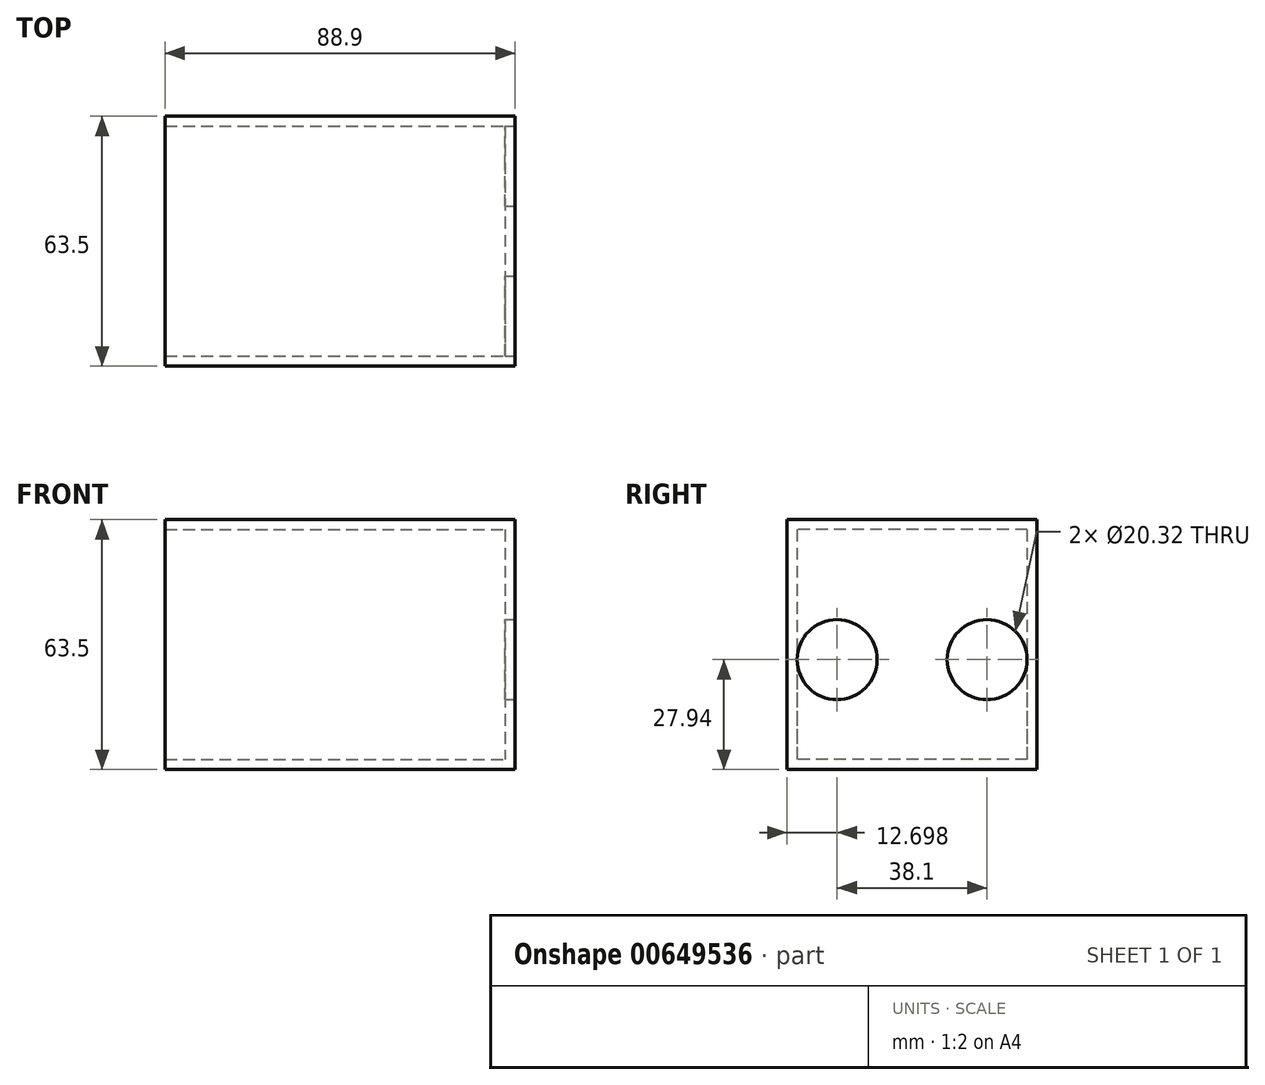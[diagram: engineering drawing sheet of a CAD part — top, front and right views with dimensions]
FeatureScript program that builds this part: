
annotation { "Feature Type Name" : "Feature", "Feature Type Description" : "" }
export const myFeature = defineFeature(function(context is Context, id is Id, definition is map)
    precondition{}
    {
        {
            var Q0;
            Q0=qCreatedBy(makeId("Top.planeOp"),FACE);
            var sketch = newSketch(context, id + "F0", { "sketchPlane" : qUnion([Q0])});
            skLineSegment(sketch, "E0.bottom", {"start": v(-33.77, 48.5) * mm, "end": v(55.13, 48.5) * mm});
            skLineSegment(sketch, "E0.top", {"start": v(-33.77, -15) * mm, "end": v(55.13, -15) * mm});
            skLineSegment(sketch, "E0.left", {"start": v(-33.77, 48.5) * mm, "end": v(-33.77, -15) * mm});
            skLineSegment(sketch, "E0.right", {"start": v(55.13, 48.5) * mm, "end": v(55.13, -15) * mm});
            skSolve(sketch);
        }
        {
            var Q0;
            Q0=makeQuery(id+"F0.imprint","IMPRINT",FACE,{"disambiguationData":[TD([[makeQuery(id+"F0.imprint","IMPRINT",EDGE,{"derivedFrom":sQuery(id+"F0.wireOp",EDGE,"E0.bottom")}),-1.0]])]});
            extrude(context, id + "F1", {"entities" : qUnion([Q0]), "depth" : 63.5 * mm, "offsetDistance" : 25.4 * mm});
        }
        {
            var Q0;
            Q0=makeQuery(id+"F1.opExtrude","SWEPT_FACE",FACE,{"disambiguationData":[OSD([sQuery(id+"F0.wireOp",EDGE,"E0.right")])]});
            var sketch = newSketch(context, id + "F2", { "sketchPlane" : qUnion([Q0])});
            skCircle(sketch, "E1", {"center": v(-2.3, 27.94) * mm, "radius": 10.16 * mm});
            skCircle(sketch, "E2", {"center": v(35.8, 27.94) * mm, "radius": 10.16 * mm});
            skSolve(sketch);
        }
        {
            var Q0;
            Q0=makeQuery(id+"F1.opExtrude","SWEPT_FACE",FACE,{"disambiguationData":[OSD([sQuery(id+"F0.wireOp",EDGE,"E0.left")])]});
            shell(context, id + "F3", {"entities" : qUnion([Q0]), "thickness" : 2.54 * mm});
        }
        {
            var Q0;
            Q0=makeQuery(id+"F2.imprint","IMPRINT",FACE,{"disambiguationData":[TD([[makeQuery(id+"F2.imprint","IMPRINT",EDGE,{"derivedFrom":sQuery(id+"F2.wireOp",EDGE,"E1")}),1.0]])]});
            var Q1;
            Q1=makeQuery(id+"F2.imprint","IMPRINT",FACE,{"disambiguationData":[TD([[makeQuery(id+"F2.imprint","IMPRINT",EDGE,{"derivedFrom":sQuery(id+"F2.wireOp",EDGE,"E2")}),1.0]])]});
            extrude(context, id + "F4", {"entities" : qUnion([Q0, Q1]), "operationType" : NewBodyOperationType.REMOVE, "oppositeDirection" : true, "depth" : 25.4 * mm, "offsetDistance" : 25.4 * mm});
        }
    });
